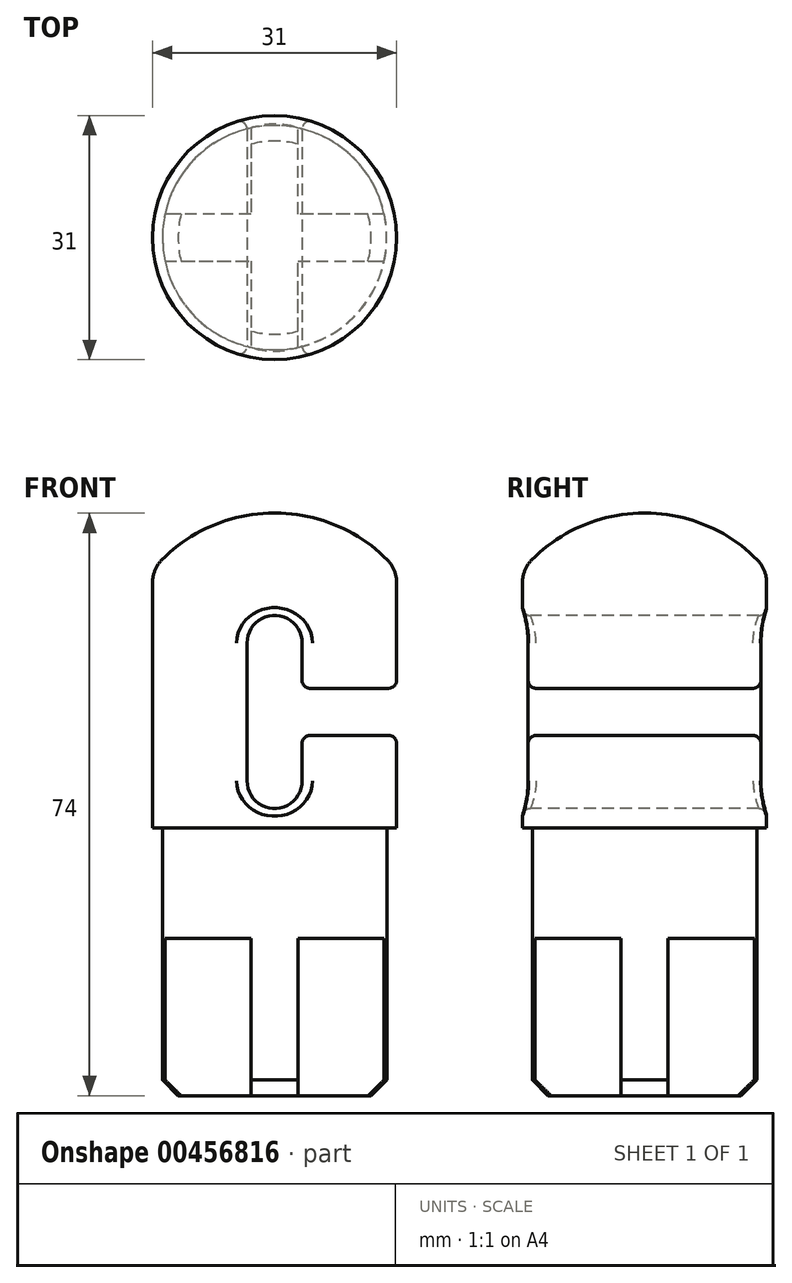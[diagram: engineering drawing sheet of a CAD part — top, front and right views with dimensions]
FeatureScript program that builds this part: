
annotation { "Feature Type Name" : "Feature", "Feature Type Description" : "" }
export const myFeature = defineFeature(function(context is Context, id is Id, definition is map)
    precondition{}
    {
        {
            var Q0;
            Q0=qCreatedBy(makeId("Top.planeOp"),FACE);
            var sketch = newSketch(context, id + "F0", { "sketchPlane" : qUnion([Q0])});
            skCircle(sketch, "E0", {"center": v(0, 0) * mm, "radius": 15.5 * mm});
            skSolve(sketch);
        }
        {
            var Q0;
            Q0 = qSketchRegion(id + "F0", true);
            extrude(context, id + "F1", {"entities" : qUnion([Q0]), "depth" : 40 * mm});
        }
        {
            var Q0;
            Q0=qCreatedBy(makeId("Front.planeOp"),FACE);
            cPlane(context, id + "F2", {"entities" : qUnion([Q0]), "cplaneType" : CPlaneType.OFFSET, "offset" : 20 * mm, "width" : 150 * mm, "height" : 150 * mm});
        }
        {
            var Q0;
            Q0=qCreatedBy(id+"F2.planeOp",FACE);
            var sketch = newSketch(context, id + "F3", { "sketchPlane" : qUnion([Q0])});
            skLineSegment(sketch, "E1", {"start": v(19.5, 17.75) * mm, "end": v(3.5, 17.75) * mm});
            skLineSegment(sketch, "E2", {"start": v(3.5, 17.75) * mm, "end": v(3.5, 23.5) * mm});
            skLineSegment(sketch, "E3", {"start": v(-3.5, 23.5) * mm, "end": v(-3.5, 6) * mm});
            skLineSegment(sketch, "E4", {"start": v(3.5, 6) * mm, "end": v(3.5, 11.75) * mm});
            skLineSegment(sketch, "E5", {"start": v(3.5, 11.75) * mm, "end": v(19.5, 11.75) * mm});
            skLineSegment(sketch, "E6", {"start": v(19.5, 11.75) * mm, "end": v(19.5, 17.75) * mm});
            skArc(sketch, "E7", {"start": v(-3.5, 23.5) * mm, "mid": v(0, 27) * mm, "end": v(3.5, 23.5) * mm});
            skArc(sketch, "E8", {"start": v(-3.5, 6) * mm, "mid": v(0, 2.5) * mm, "end": v(3.5, 6) * mm});
            skSolve(sketch);
        }
        {
            var Q0;
            Q0=makeQuery(id+"F3.imprint","IMPRINT",FACE,{"disambiguationData":[TD([[makeQuery(id+"F3.imprint","IMPRINT",EDGE,{"derivedFrom":sQuery(id+"F3.wireOp",EDGE,"E1")}),1.0]])]});
            extrude(context, id + "F4", {"entities" : qUnion([Q0]), "operationType" : NewBodyOperationType.REMOVE, "oppositeDirection" : true, "depth" : 40 * mm});
        }
        {
            var Q0;
            Q0=makeQuery(id+"F4.boolean.opBoolean","INTERSECT",EDGE,{"disambiguationData":[OD(0.0)],"derivedFrom":[makeQuery(id+"F1.opExtrude","SWEPT_FACE",FACE,{"disambiguationData":[OSD([sQuery(id+"F0.wireOp",EDGE,"E0")])]}),makeQuery(id+"F4.opExtrude","SWEPT_FACE",FACE,{"disambiguationData":[OSD([sQuery(id+"F3.wireOp",EDGE,"E7")])]})]});
            var Q1;
            Q1=makeQuery(id+"F4.boolean.opBoolean","INTERSECT",EDGE,{"derivedFrom":[makeQuery(id+"F1.opExtrude","SWEPT_FACE",FACE,{"disambiguationData":[OSD([sQuery(id+"F0.wireOp",EDGE,"E0")])]}),makeQuery(id+"F4.opExtrude","SWEPT_FACE",FACE,{"disambiguationData":[OSD([sQuery(id+"F3.wireOp",EDGE,"E1")])]})]});
            var Q2;
            Q2=makeQuery(id+"F4.boolean.opBoolean","INTERSECT",EDGE,{"derivedFrom":[makeQuery(id+"F1.opExtrude","SWEPT_FACE",FACE,{"disambiguationData":[OSD([sQuery(id+"F0.wireOp",EDGE,"E0")])]}),makeQuery(id+"F4.opExtrude","SWEPT_FACE",FACE,{"disambiguationData":[OSD([sQuery(id+"F3.wireOp",EDGE,"E5")])]})]});
            var Q3;
            Q3=makeQuery(id+"F4.boolean.opBoolean","INTERSECT",EDGE,{"disambiguationData":[OD(1.0)],"derivedFrom":[makeQuery(id+"F1.opExtrude","SWEPT_FACE",FACE,{"disambiguationData":[OSD([sQuery(id+"F0.wireOp",EDGE,"E0")])]}),makeQuery(id+"F4.opExtrude","SWEPT_FACE",FACE,{"disambiguationData":[OSD([sQuery(id+"F3.wireOp",EDGE,"E3")])]})]});
            var Q4;
            Q4=makeQuery(id+"F4.boolean.opBoolean","COPY",EDGE,{"derivedFrom":makeQuery(id+"F4.opExtrude","SWEPT_EDGE",EDGE,{"disambiguationData":[OSD([sQuery(id+"F3.wireOp",EDGE,"E1"),sQuery(id+"F3.wireOp",EDGE,"E2")])]})});
            var Q5;
            Q5=makeQuery(id+"F4.boolean.opBoolean","COPY",EDGE,{"derivedFrom":makeQuery(id+"F4.opExtrude","SWEPT_EDGE",EDGE,{"disambiguationData":[OSD([sQuery(id+"F3.wireOp",EDGE,"E4"),sQuery(id+"F3.wireOp",EDGE,"E5")])]})});
            fillet(context, id + "F5", {"entities" : qUnion([Q0, Q1, Q2, Q3, Q4, Q5]), "radius" : 1 * mm, "tangentPropagation" : true, "allowEdgeOverflow" : false});
        }
        {
            var Q0;
            Q0=makeQuery(id+"F1.opExtrude","CAP_FACE",FACE,{"disambiguationData":[OSD([sQuery(id+"F0.wireOp",EDGE,"E0")])],"isStart":true});
            var sketch = newSketch(context, id + "F6", { "sketchPlane" : qUnion([Q0])});
            skCircle(sketch, "E9", {"center": v(0, 0) * mm, "radius": 14.25 * mm});
            skSolve(sketch);
        }
        {
            var Q0;
            Q0=makeQuery(id+"F6.imprint","IMPRINT",FACE,{"disambiguationData":[TD([[makeQuery(id+"F6.imprint","IMPRINT",EDGE,{"derivedFrom":sQuery(id+"F6.wireOp",EDGE,"E9")}),1.0]])]});
            extrude(context, id + "F7", {"entities" : qUnion([Q0]), "operationType" : NewBodyOperationType.ADD, "depth" : 34 * mm});
        }
        {
            var Q0;
            Q0=makeQuery(id+"F7.opExtrude","CAP_EDGE",EDGE,{"disambiguationData":[OSD([sQuery(id+"F6.wireOp",EDGE,"E9")])],"isStart":false});
            chamfer(context, id + "F8", {"entities" : qUnion([Q0]), "width" : 2 * mm, "tangentPropagation" : true});
        }
        {
            var Q0;
            Q0=makeQuery(id+"F7.opExtrude","CAP_FACE",FACE,{"disambiguationData":[OSD([sQuery(id+"F6.wireOp",EDGE,"E9")])],"isStart":false});
            var sketch = newSketch(context, id + "F9", { "sketchPlane" : qUnion([Q0])});
            skLineSegment(sketch, "E10", {"start": v(3, 3) * mm, "end": v(33.33, 3) * mm});
            skLineSegment(sketch, "E11", {"start": v(33.33, 3) * mm, "end": v(3, 21.45) * mm});
            skLineSegment(sketch, "E12", {"start": v(3, 21.45) * mm, "end": v(3, 3) * mm});
            skLineSegment(sketch, "E13", {"start": v(-3, 3) * mm, "end": v(-3, 21.45) * mm});
            skLineSegment(sketch, "E14", {"start": v(-3, 21.45) * mm, "end": v(-23, 3) * mm});
            skLineSegment(sketch, "E15", {"start": v(-23, 3) * mm, "end": v(-3, 3) * mm});
            skLineSegment(sketch, "E16", {"start": v(-3, -3) * mm, "end": v(-23, -3) * mm});
            skLineSegment(sketch, "E17", {"start": v(-23, -3) * mm, "end": v(-3, -23) * mm});
            skLineSegment(sketch, "E18", {"start": v(-3, -23) * mm, "end": v(-3, -3) * mm});
            skLineSegment(sketch, "E19", {"start": v(3, -3) * mm, "end": v(3, -23) * mm});
            skLineSegment(sketch, "E20", {"start": v(3, -23) * mm, "end": v(33.33, -3) * mm});
            skLineSegment(sketch, "E21", {"start": v(33.33, -3) * mm, "end": v(3, -3) * mm});
            skSolve(sketch);
        }
        {
            var Q0;
            Q0 = qSketchRegion(id + "F9", true);
            extrude(context, id + "F10", {"entities" : qUnion([Q0]), "operationType" : NewBodyOperationType.REMOVE, "oppositeDirection" : true, "depth" : 20 * mm});
        }
        {
            var Q0;
            Q0=qCreatedBy(makeId("Front.planeOp"),FACE);
            var sketch = newSketch(context, id + "F11", { "sketchPlane" : qUnion([Q0])});
            skArc(sketch, "E22", {"start": v(20.1, 20) * mm, "mid": v(14.24, 34.14) * mm, "end": v(0.1, 40) * mm});
            skLineSegment(sketch, "E23", {"start": v(0.1, 40) * mm, "end": v(20.1, 40) * mm});
            skLineSegment(sketch, "E24", {"start": v(20.1, 40) * mm, "end": v(20.1, 20) * mm});
            skLineSegment(sketch, "E25", {"start": v(0, 0) * mm, "end": v(0, 40) * mm, "construction": true});
            skSolve(sketch);
        }
        {
            var Q0;
            Q0 = qSketchRegion(id + "F11", true);
            var Q1;
            Q1=sQuery(id+"F11.wireOp",EDGE,"E25");
            revolve(context, id + "F12", {"operationType" : NewBodyOperationType.REMOVE, "entities" : qUnion([Q0]), "axis" : qUnion([Q1]), "revolveType" : RevolveType.FULL, "oppositeDirection" : true});
        }
        {
            var Q0;
            Q0=makeQuery(id+"F12.boolean.opBoolean","INTERSECT",EDGE,{"derivedFrom":[makeQuery(id+"F1.opExtrude","SWEPT_FACE",FACE,{"disambiguationData":[OSD([sQuery(id+"F0.wireOp",EDGE,"E0")])]}),makeQuery(id+"F12.opRevolve","SWEPT_FACE",FACE,{"disambiguationData":[OSD([sQuery(id+"F11.wireOp",EDGE,"E22")])]})]});
            fillet(context, id + "F13", {"entities" : qUnion([Q0]), "radius" : 4 * mm, "tangentPropagation" : true, "allowEdgeOverflow" : false});
        }
    });
